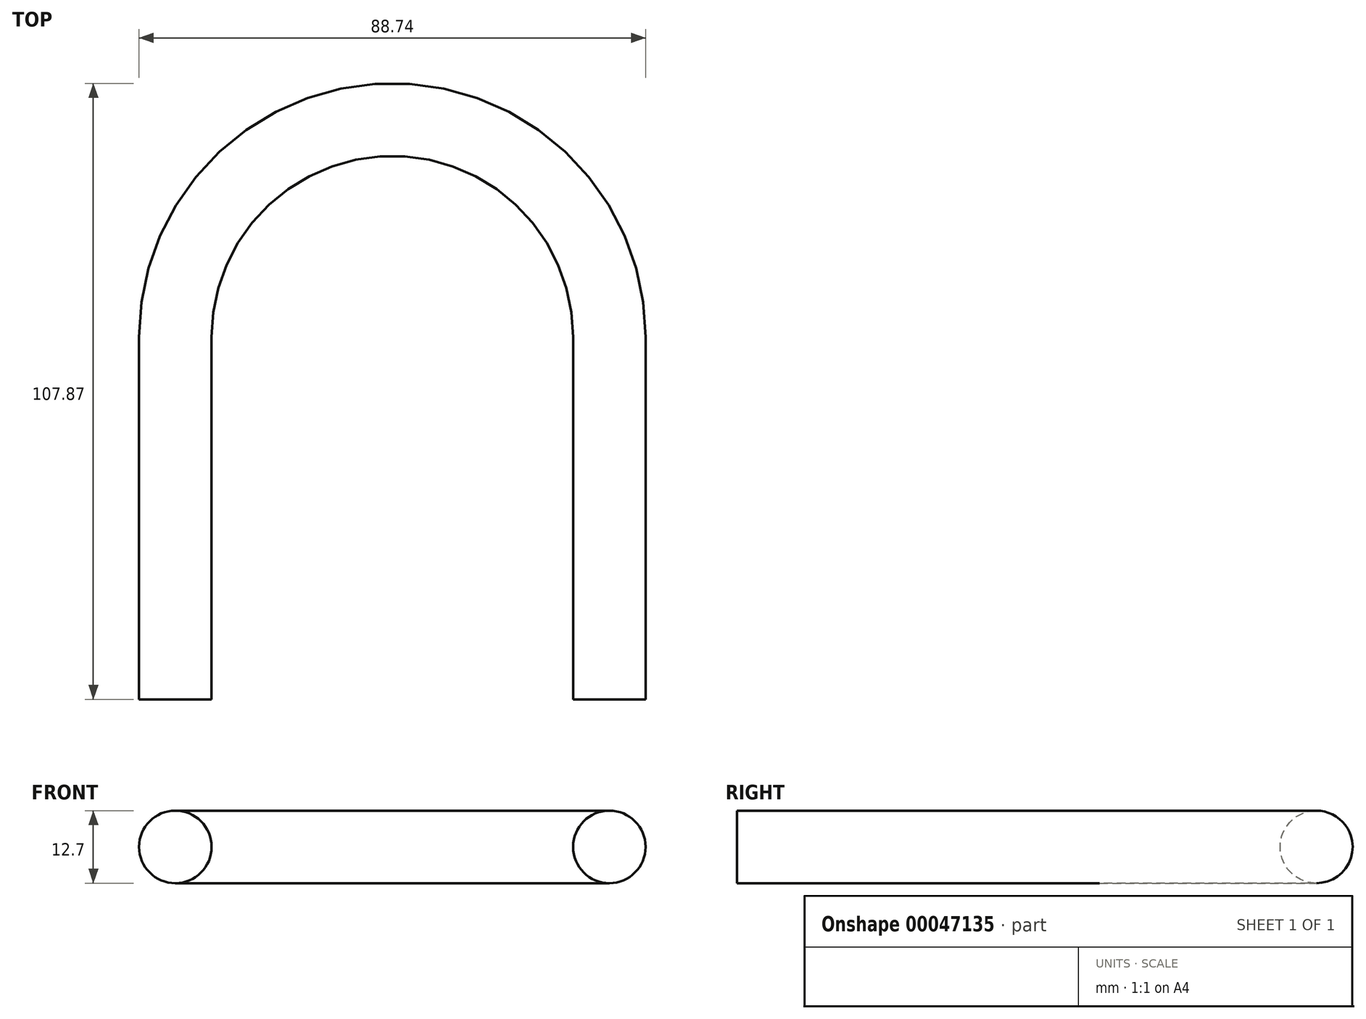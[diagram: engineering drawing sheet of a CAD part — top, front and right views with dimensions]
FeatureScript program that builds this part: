
annotation { "Feature Type Name" : "Feature", "Feature Type Description" : "" }
export const myFeature = defineFeature(function(context is Context, id is Id, definition is map)
    precondition{}
    {
        {
            var Q0;
            Q0=qCreatedBy(makeId("Top.planeOp"),FACE);
            var sketch = newSketch(context, id + "F0", { "sketchPlane" : qUnion([Q0])});
            skLineSegment(sketch, "E0", {"start": v(0, 0) * mm, "end": v(0, 63.5) * mm});
            skArc(sketch, "E1", {"start": v(0, 63.5) * mm, "mid": v(-38.1, 101.6) * mm, "end": v(-76.2, 63.5) * mm});
            skLineSegment(sketch, "E2", {"start": v(-76.2, 63.5) * mm, "end": v(-76.2, 0) * mm});
            skSolve(sketch);
        }
        {
            var Q0;
            Q0=qCreatedBy(makeId("Front.planeOp"),FACE);
            var sketch = newSketch(context, id + "F1", { "sketchPlane" : qUnion([Q0])});
            skCircle(sketch, "E3", {"center": v(-0.08, -0.1) * mm, "radius": 6.35 * mm});
            skSolve(sketch);
        }
        {
            var Q0;
            Q0=makeQuery(id+"F1.imprint","IMPRINT",FACE,{"disambiguationData":[TD([[makeQuery(id+"F1.imprint","IMPRINT",EDGE,{"derivedFrom":sQuery(id+"F1.wireOp",EDGE,"E3")}),1.0]])]});
            var Q1;
            Q1=sQuery(id+"F0.wireOp",EDGE,"E0");
            var Q2;
            Q2=sQuery(id+"F0.wireOp",EDGE,"E1");
            var Q3;
            Q3=sQuery(id+"F0.wireOp",EDGE,"E2");
            sweep(context, id + "F2", {"profiles" : qUnion([Q0]), "path" : qUnion([Q1, Q2, Q3])});
        }
    });
